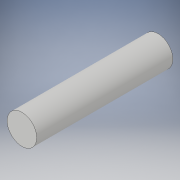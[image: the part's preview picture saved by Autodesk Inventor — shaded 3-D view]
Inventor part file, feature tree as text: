
AUTODESK INVENTOR PART (.ipt)
format: ipt  version: 2019 (Build 230136000, 136)  size: 90,112 bytes
history: native  units: mm
features: extrude x1, sketch x1
ambient origin geometry x8: Origin, YZ Plane, XZ Plane, XY Plane, X Axis, Y Axis, Z Axis, Center Point
bodies: Solid1 (feature_tree)
feature tree (2):
  extrude  "Extrusion1"  Depth=23.0mm TaperAngle=0.0deg
  sketch  "Sketch1"  dims[d0=5.0mm d1=23.0mm d2=0.0mm]
